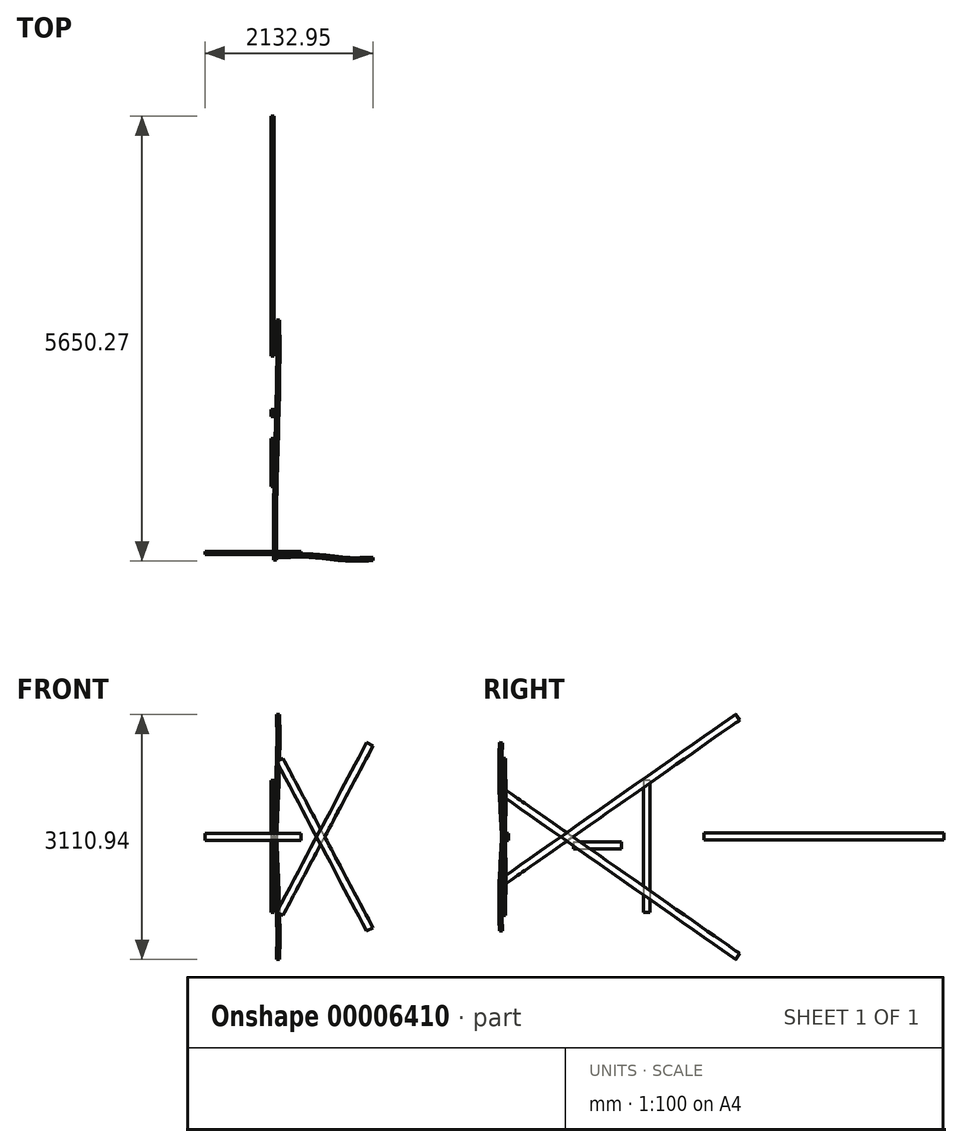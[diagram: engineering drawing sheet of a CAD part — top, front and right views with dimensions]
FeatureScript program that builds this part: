
annotation { "Feature Type Name" : "Feature", "Feature Type Description" : "" }
export const myFeature = defineFeature(function(context is Context, id is Id, definition is map)
    precondition{}
    {
        {
            var Q0;
            Q0=qCreatedBy(makeId("Right.planeOp"),FACE);
            var sketch = newSketch(context, id + "F0", { "sketchPlane" : qUnion([Q0])});
            skLineSegment(sketch, "E0", {"start": v(-58.65, 614) * mm, "end": v(2938.4, -1482.62) * mm});
            skLineSegment(sketch, "E1", {"start": v(2938.4, -1482.62) * mm, "end": v(2989.35, -1409.78) * mm});
            skLineSegment(sketch, "E2", {"start": v(2989.35, -1409.78) * mm, "end": v(-7.69, 686.84) * mm});
            skLineSegment(sketch, "E3", {"start": v(-7.69, 686.84) * mm, "end": v(-58.65, 614) * mm});
            skSolve(sketch);
        }
        {
            var Q0;
            Q0 = qSketchRegion(id + "F0", true);
            extrude(context, id + "F1", {"entities" : qUnion([Q0]), "depth" : 38.1 * mm});
        }
        {
            var Q0;
            Q0=makeQuery(id+"F1.opExtrude","SWEPT_FACE",FACE,{"disambiguationData":[OSD([sQuery(id+"F0.wireOp",EDGE,"E0")])]});
            var sketch = newSketch(context, id + "F2", { "sketchPlane" : qUnion([Q0])});
            skFitSpline(sketch, "E4", {"points": [v(31.94, 400) * mm, v(31.94, -540.6) * mm, v(70.04, -2498.39) * mm, v(70.04, -3257.6) * mm], "startDerivative": vector(-16.35, -638.16) * mm, "endDerivative": vector(14.76, -413.57) * mm});
            skSolve(sketch);
        }
        {
            var Q0;
            Q0=sQuery(id+"F2.wireOp",VERTEX,"E4.start");
            var Q1;
            Q1=sQuery(id+"F2.wireOp",EDGE,"E4");
            cPlane(context, id + "F3", {"entities" : qUnion([Q0, Q1]), "cplaneType" : CPlaneType.CURVE_POINT, "offset" : 152.4 * mm, "width" : 152.4 * mm, "height" : 152.4 * mm});
        }
        {
            var Q0;
            Q0=qCreatedBy(id+"F3.planeOp",FACE);
            var sketch = newSketch(context, id + "F4", { "sketchPlane" : qUnion([Q0])});
            skLineSegment(sketch, "E5.bottom", {"start": v(-21.68, 469.49) * mm, "end": v(-59.78, 469.49) * mm});
            skLineSegment(sketch, "E5.top", {"start": v(-21.68, 380.59) * mm, "end": v(-59.78, 380.59) * mm});
            skLineSegment(sketch, "E5.left", {"start": v(-21.68, 469.49) * mm, "end": v(-21.68, 380.59) * mm});
            skLineSegment(sketch, "E5.right", {"start": v(-59.78, 469.49) * mm, "end": v(-59.78, 380.59) * mm});
            skPoint(sketch, "E6.0", {"position": v(-21.68, 469.49) * mm});
            skSolve(sketch);
        }
        {
            var Q0;
            Q0=makeQuery(id+"F4.imprint","IMPRINT",FACE,{"disambiguationData":[TD([[makeQuery(id+"F4.imprint","IMPRINT",EDGE,{"derivedFrom":sQuery(id+"F4.wireOp",EDGE,"E5.bottom")}),1.0]])]});
            var Q1;
            Q1=sQuery(id+"F2.wireOp",EDGE,"E4");
            sweep(context, id + "F5", {"profiles" : qUnion([Q0]), "path" : qUnion([Q1])});
        }
        {
            var Q0;
            Q0=makeQuery(id+"F1.opExtrude","SWEPT_BODY",BODY,{"disambiguationData":[OSD([sQuery(id+"F0.wireOp",EDGE,"E0"),sQuery(id+"F0.wireOp",EDGE,"E1"),sQuery(id+"F0.wireOp",EDGE,"E2"),sQuery(id+"F0.wireOp",EDGE,"E3")])]});
            deleteBodies(context, id + "F6", {"entities" : qUnion([Q0])});
        }
        {
            var Q0;
            Q0=makeQuery(id+"F5.opSweep","SWEPT_BODY",BODY,{"disambiguationData":[OSD([sQuery(id+"F2.wireOp",EDGE,"E4"),sQuery(id+"F4.wireOp",EDGE,"E5.bottom"),sQuery(id+"F4.wireOp",EDGE,"E5.top"),sQuery(id+"F4.wireOp",EDGE,"E5.left"),sQuery(id+"F4.wireOp",EDGE,"E5.right")])]});
            var Q1;
            Q1=qCreatedBy(makeId("Top.planeOp"),FACE);
            mirror(context, id + "F7", {"entities" : qUnion([Q0]), "mirrorPlane" : qUnion([Q1])});
        }
        {
            var Q0;
            Q0=qCreatedBy(makeId("Front.planeOp"),FACE);
            var sketch = newSketch(context, id + "F8", { "sketchPlane" : qUnion([Q0])});
            skLineSegment(sketch, "E7", {"start": v(298.65, 716.06) * mm, "end": v(1441.65, -1437.86) * mm});
            skLineSegment(sketch, "E8", {"start": v(1441.65, -1437.86) * mm, "end": v(154.45, -1437.86) * mm});
            skSolve(sketch);
        }
        {
            var Q0;
            Q0=sQuery(id+"F8.wireOp",EDGE,"E7");
            cPlane(context, id + "F9", {"entities" : qUnion([Q0]), "cplaneType" : CPlaneType.LINE_ANGLE, "offset" : 152.4 * mm, "angle" : 0 * degree, "width" : 152.4 * mm, "height" : 152.4 * mm});
        }
        {
            var Q0;
            Q0=qCreatedBy(id+"F9.planeOp",FACE);
            var sketch = newSketch(context, id + "F10", { "sketchPlane" : qUnion([Q0])});
            skFitSpline(sketch, "E9", {"points": [v(39.44, 813.37) * mm, v(39.44, -150.6) * mm, v(77.54, -924.59) * mm, v(77.54, -1625.03) * mm], "startDerivative": vector(-61.83, -2825.96) * mm, "endDerivative": vector(-56.55, -2617.11) * mm});
            skSolve(sketch);
        }
        {
            var Q0;
            Q0=sQuery(id+"F10.wireOp",EDGE,"E9");
            var Q1;
            Q1=sQuery(id+"F10.wireOp",VERTEX,"E9.start");
            cPlane(context, id + "F11", {"entities" : qUnion([Q0, Q1]), "cplaneType" : CPlaneType.CURVE_POINT, "offset" : 152.4 * mm, "width" : 152.4 * mm, "height" : 152.4 * mm});
        }
        {
            var Q0;
            Q0=qCreatedBy(id+"F11.planeOp",FACE);
            var sketch = newSketch(context, id + "F12", { "sketchPlane" : qUnion([Q0])});
            skLineSegment(sketch, "E10.bottom", {"start": v(510.77, 52.78) * mm, "end": v(599.67, 52.78) * mm});
            skLineSegment(sketch, "E10.top", {"start": v(510.77, 14.68) * mm, "end": v(599.67, 14.68) * mm});
            skLineSegment(sketch, "E10.left", {"start": v(510.77, 52.78) * mm, "end": v(510.77, 14.68) * mm});
            skLineSegment(sketch, "E10.right", {"start": v(599.67, 52.78) * mm, "end": v(599.67, 14.68) * mm});
            skSolve(sketch);
        }
        {
            var Q0;
            Q0=makeQuery(id+"F12.imprint","IMPRINT",FACE,{"disambiguationData":[TD([[makeQuery(id+"F12.imprint","IMPRINT",EDGE,{"derivedFrom":sQuery(id+"F12.wireOp",EDGE,"E10.bottom")}),-1.0]])]});
            var Q1;
            Q1=sQuery(id+"F10.wireOp",EDGE,"E9");
            sweep(context, id + "F13", {"profiles" : qUnion([Q0]), "path" : qUnion([Q1])});
        }
        {
            var Q0;
            Q0=makeQuery(id+"F13.opSweep","SWEPT_BODY",BODY,{"disambiguationData":[OSD([sQuery(id+"F10.wireOp",EDGE,"E9"),sQuery(id+"F12.wireOp",EDGE,"E10.bottom"),sQuery(id+"F12.wireOp",EDGE,"E10.top"),sQuery(id+"F12.wireOp",EDGE,"E10.left"),sQuery(id+"F12.wireOp",EDGE,"E10.right")])]});
            var Q1;
            Q1=qCreatedBy(makeId("Top.planeOp"),FACE);
            mirror(context, id + "F14", {"entities" : qUnion([Q0]), "mirrorPlane" : qUnion([Q1])});
        }
        {
            var Q0;
            Q0=qCreatedBy(makeId("Right.planeOp"),FACE);
            var sketch = newSketch(context, id + "F15", { "sketchPlane" : qUnion([Q0])});
            skLineSegment(sketch, "E11.bottom", {"start": v(2481.35, 52.5) * mm, "end": v(5529.35, 52.5) * mm});
            skLineSegment(sketch, "E11.top", {"start": v(2481.35, -36.4) * mm, "end": v(5529.35, -36.4) * mm});
            skLineSegment(sketch, "E11.left", {"start": v(2481.35, 52.5) * mm, "end": v(2481.35, -36.4) * mm});
            skLineSegment(sketch, "E11.right", {"start": v(5529.35, 52.5) * mm, "end": v(5529.35, -36.4) * mm});
            skSolve(sketch);
        }
        {
            var Q0;
            Q0 = qSketchRegion(id + "F15", true);
            extrude(context, id + "F16", {"entities" : qUnion([Q0]), "depth" : 38.1 * mm});
        }
        {
            var Q0;
            Q0=qCreatedBy(makeId("Front.planeOp"),FACE);
            var sketch = newSketch(context, id + "F17", { "sketchPlane" : qUnion([Q0])});
            skLineSegment(sketch, "E12.bottom", {"start": v(377.5, 41.64) * mm, "end": v(-841.7, 41.64) * mm});
            skLineSegment(sketch, "E12.top", {"start": v(377.5, -47.26) * mm, "end": v(-841.7, -47.26) * mm});
            skLineSegment(sketch, "E12.left", {"start": v(377.5, 41.64) * mm, "end": v(377.5, -47.26) * mm});
            skLineSegment(sketch, "E12.right", {"start": v(-841.7, 41.64) * mm, "end": v(-841.7, -47.26) * mm});
            skSolve(sketch);
        }
        {
            var Q0;
            Q0 = qSketchRegion(id + "F17", true);
            extrude(context, id + "F18", {"entities" : qUnion([Q0]), "depth" : 38.1 * mm});
        }
        {
            var Q0;
            Q0=qCreatedBy(makeId("Right.planeOp"),FACE);
            var sketch = newSketch(context, id + "F19", { "sketchPlane" : qUnion([Q0])});
            skLineSegment(sketch, "E13.bottom", {"start": v(824.82, -61.77) * mm, "end": v(1434.42, -61.77) * mm});
            skLineSegment(sketch, "E13.top", {"start": v(824.82, -150.67) * mm, "end": v(1434.42, -150.67) * mm});
            skLineSegment(sketch, "E13.left", {"start": v(824.82, -61.77) * mm, "end": v(824.82, -150.67) * mm});
            skLineSegment(sketch, "E13.right", {"start": v(1434.42, -61.77) * mm, "end": v(1434.42, -150.67) * mm});
            skSolve(sketch);
        }
        {
            var Q0;
            Q0 = qSketchRegion(id + "F19", true);
            extrude(context, id + "F20", {"entities" : qUnion([Q0]), "depth" : 38.1 * mm});
        }
        {
            var Q0;
            Q0=qCreatedBy(makeId("Right.planeOp"),FACE);
            var sketch = newSketch(context, id + "F21", { "sketchPlane" : qUnion([Q0])});
            skLineSegment(sketch, "E14.bottom", {"start": v(1801.6, 718.38) * mm, "end": v(1712.7, 718.38) * mm});
            skLineSegment(sketch, "E14.top", {"start": v(1801.6, -958.02) * mm, "end": v(1712.7, -958.02) * mm});
            skLineSegment(sketch, "E14.left", {"start": v(1801.6, 718.38) * mm, "end": v(1801.6, -958.02) * mm});
            skLineSegment(sketch, "E14.right", {"start": v(1712.7, 718.38) * mm, "end": v(1712.7, -958.02) * mm});
            skSolve(sketch);
        }
        {
            var Q0;
            Q0 = qSketchRegion(id + "F21", true);
            extrude(context, id + "F22", {"entities" : qUnion([Q0]), "depth" : 38.1 * mm});
        }
    });
